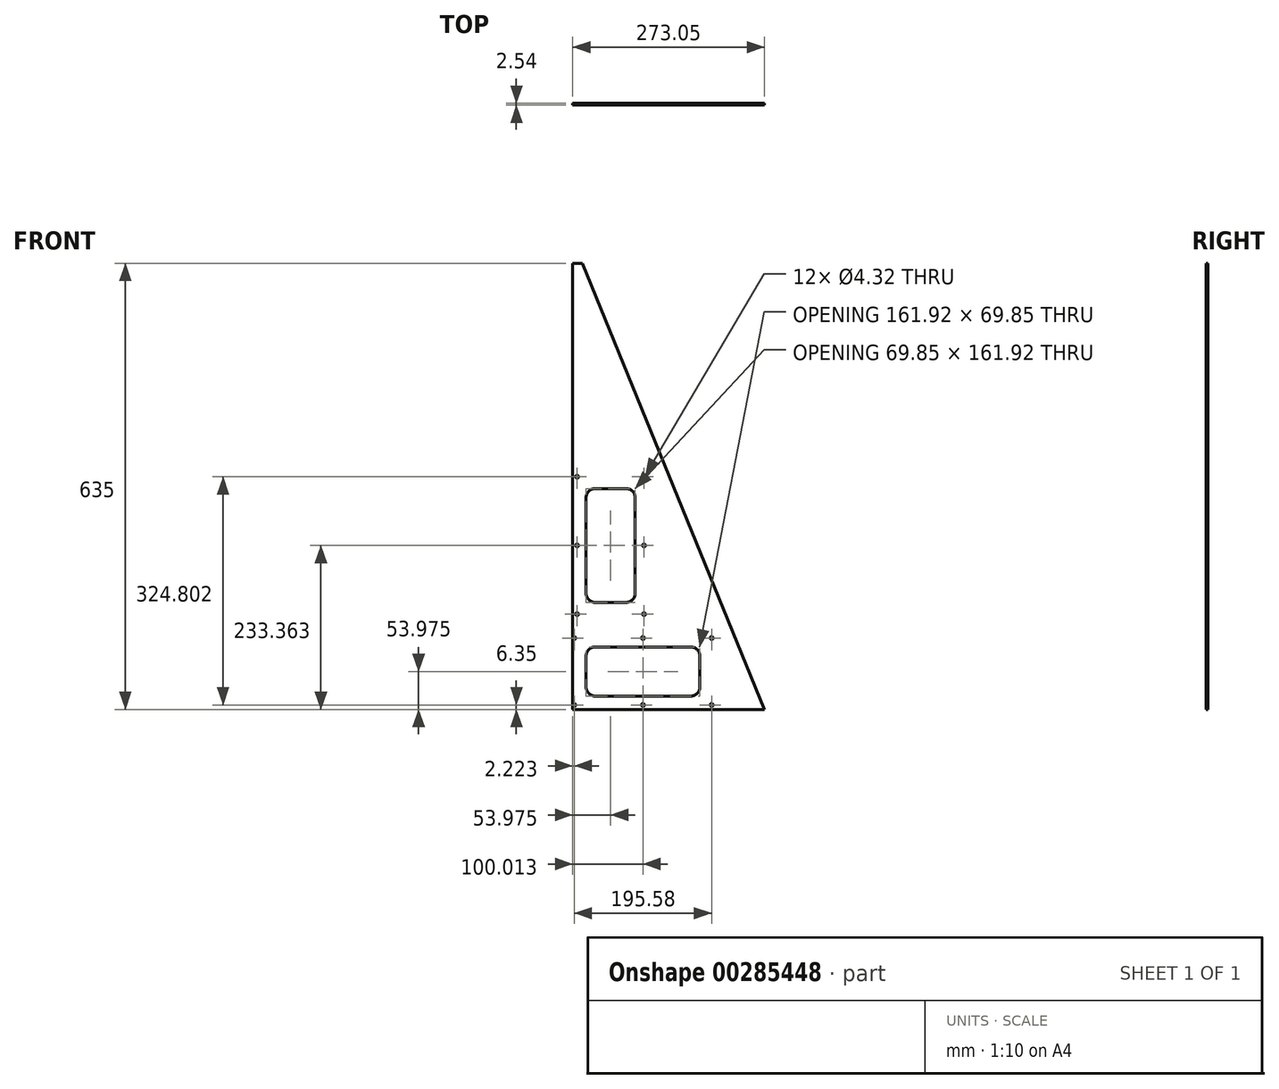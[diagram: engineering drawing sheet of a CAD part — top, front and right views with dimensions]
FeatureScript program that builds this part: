
annotation { "Feature Type Name" : "Feature", "Feature Type Description" : "" }
export const myFeature = defineFeature(function(context is Context, id is Id, definition is map)
    precondition{}
    {
        {
            var Q0;
            Q0=qCreatedBy(makeId("Front.planeOp"),FACE);
            var sketch = newSketch(context, id + "F0", { "sketchPlane" : qUnion([Q0])});
            skLineSegment(sketch, "E0", {"start": v(0, 0) * mm, "end": v(0, 635) * mm});
            skArc(sketch, "E1.MirrorCS", {"start": v(31.75, 19.05) * mm, "mid": v(22.77, 22.77) * mm, "end": v(19.05, 31.75) * mm});
            skArc(sketch, "E2.MirrorCS", {"start": v(168.28, 88.9) * mm, "mid": v(177.26, 85.18) * mm, "end": v(180.97, 76.2) * mm});
            skArc(sketch, "E3.MirrorCS", {"start": v(19.05, 76.2) * mm, "mid": v(22.77, 85.18) * mm, "end": v(31.75, 88.9) * mm});
            skArc(sketch, "E4.MirrorCS", {"start": v(31.75, 152.4) * mm, "mid": v(22.77, 156.12) * mm, "end": v(19.05, 165.1) * mm});
            skArc(sketch, "E5.MirrorCS", {"start": v(19.05, 301.63) * mm, "mid": v(22.77, 310.6) * mm, "end": v(31.75, 314.33) * mm});
            skArc(sketch, "E6.MirrorCS", {"start": v(180.97, 31.75) * mm, "mid": v(177.26, 22.77) * mm, "end": v(168.28, 19.05) * mm});
            skArc(sketch, "E7.MirrorCS", {"start": v(76.2, 314.33) * mm, "mid": v(85.18, 310.6) * mm, "end": v(88.9, 301.63) * mm});
            skArc(sketch, "E8.MirrorCS", {"start": v(88.9, 165.1) * mm, "mid": v(85.18, 156.12) * mm, "end": v(76.2, 152.4) * mm});
            skLineSegment(sketch, "E9.MirrorCS", {"start": v(0, 635) * mm, "end": v(14.02, 635) * mm});
            skLineSegment(sketch, "E10.MirrorCS", {"start": v(76.2, 152.4) * mm, "end": v(31.75, 152.4) * mm});
            skLineSegment(sketch, "E11.MirrorCS", {"start": v(180.97, 76.2) * mm, "end": v(180.97, 31.75) * mm});
            skLineSegment(sketch, "E12.MirrorCS", {"start": v(168.28, 88.9) * mm, "end": v(31.75, 88.9) * mm});
            skLineSegment(sketch, "E13.MirrorCS", {"start": v(19.05, 76.2) * mm, "end": v(19.05, 31.75) * mm});
            skLineSegment(sketch, "E14.MirrorCS", {"start": v(273.05, 0) * mm, "end": v(0, 0) * mm});
            skLineSegment(sketch, "E15.MirrorCS", {"start": v(168.28, 19.05) * mm, "end": v(31.75, 19.05) * mm});
            skLineSegment(sketch, "E16.MirrorCS", {"start": v(14.02, 635) * mm, "end": v(273.05, 0) * mm});
            skLineSegment(sketch, "E17.MirrorCS", {"start": v(76.2, 314.33) * mm, "end": v(31.75, 314.33) * mm});
            skPoint(sketch, "E18.MirrorP", {"position": v(19.05, 301.63) * mm});
            skLineSegment(sketch, "E19.MirrorCS", {"start": v(88.9, 165.1) * mm, "end": v(88.9, 301.63) * mm});
            skPoint(sketch, "E20.MirrorP", {"position": v(88.9, 301.63) * mm});
            skLineSegment(sketch, "E21.MirrorCS", {"start": v(19.05, 165.1) * mm, "end": v(19.05, 301.63) * mm});
            skSolve(sketch);
        }
        {
            var Q0;
            Q0=qSketchRegion(id+"F0",true);
            extrude(context, id + "F1", {"entities" : qUnion([Q0]), "depth" : 2.54 * mm});
        }
        {
            var Q0;
            Q0=makeQuery(id+"F1.opExtrude","CAP_FACE",FACE,{"disambiguationData":[OSD([sQuery(id+"F0.wireOp",EDGE,"E0"),sQuery(id+"F0.wireOp",EDGE,"E1.MirrorCS"),sQuery(id+"F0.wireOp",EDGE,"E2.MirrorCS"),sQuery(id+"F0.wireOp",EDGE,"E3.MirrorCS"),sQuery(id+"F0.wireOp",EDGE,"E4.MirrorCS"),sQuery(id+"F0.wireOp",EDGE,"E5.MirrorCS"),sQuery(id+"F0.wireOp",EDGE,"E6.MirrorCS"),sQuery(id+"F0.wireOp",EDGE,"E7.MirrorCS"),sQuery(id+"F0.wireOp",EDGE,"E8.MirrorCS"),sQuery(id+"F0.wireOp",EDGE,"E9.MirrorCS"),sQuery(id+"F0.wireOp",EDGE,"E10.MirrorCS"),sQuery(id+"F0.wireOp",EDGE,"E11.MirrorCS"),sQuery(id+"F0.wireOp",EDGE,"E12.MirrorCS"),sQuery(id+"F0.wireOp",EDGE,"E13.MirrorCS"),sQuery(id+"F0.wireOp",EDGE,"E14.MirrorCS"),sQuery(id+"F0.wireOp",EDGE,"E15.MirrorCS"),sQuery(id+"F0.wireOp",EDGE,"E16.MirrorCS"),sQuery(id+"F0.wireOp",EDGE,"E17.MirrorCS"),sQuery(id+"F0.wireOp",EDGE,"E19.MirrorCS"),sQuery(id+"F0.wireOp",EDGE,"E21.MirrorCS")])],"isStart":false});
            var sketch = newSketch(context, id + "F2", { "sketchPlane" : qUnion([Q0])});
            skPoint(sketch, "E22", {"position": v(2.22, 101.6) * mm});
            skPoint(sketch, "E23", {"position": v(100.01, 101.6) * mm});
            skPoint(sketch, "E24", {"position": v(197.8, 101.6) * mm});
            skPoint(sketch, "E25", {"position": v(197.8, 6.35) * mm});
            skPoint(sketch, "E26", {"position": v(100.01, 6.35) * mm});
            skPoint(sketch, "E27", {"position": v(2.22, 6.35) * mm});
            skLineSegment(sketch, "E28", {"start": v(100.01, 88.9) * mm, "end": v(100.01, 19.05) * mm, "construction": true});
            skPoint(sketch, "E29", {"position": v(6.35, 135.57) * mm});
            skPoint(sketch, "E30", {"position": v(6.35, 233.36) * mm});
            skPoint(sketch, "E31", {"position": v(6.35, 331.15) * mm});
            skPoint(sketch, "E32", {"position": v(101.6, 331.15) * mm});
            skPoint(sketch, "E33", {"position": v(101.6, 233.36) * mm});
            skPoint(sketch, "E34", {"position": v(101.6, 135.57) * mm});
            skLineSegment(sketch, "E35", {"start": v(19.05, 233.36) * mm, "end": v(88.9, 233.36) * mm, "construction": true});
            skSolve(sketch);
        }
        {
            var Q0;
            Q0=sQuery(id+"F2.wireOp",VERTEX,"E31");
            var Q1;
            Q1=sQuery(id+"F2.wireOp",VERTEX,"E32");
            var Q2;
            Q2=sQuery(id+"F2.wireOp",VERTEX,"E33");
            var Q3;
            Q3=sQuery(id+"F2.wireOp",VERTEX,"E30");
            var Q4;
            Q4=sQuery(id+"F2.wireOp",VERTEX,"E29");
            var Q5;
            Q5=sQuery(id+"F2.wireOp",VERTEX,"E34");
            var Q6;
            Q6=sQuery(id+"F2.wireOp",VERTEX,"E22");
            var Q7;
            Q7=sQuery(id+"F2.wireOp",VERTEX,"E27");
            var Q8;
            Q8=sQuery(id+"F2.wireOp",VERTEX,"E26");
            var Q9;
            Q9=sQuery(id+"F2.wireOp",VERTEX,"E23");
            var Q10;
            Q10=sQuery(id+"F2.wireOp",VERTEX,"E24");
            var Q11;
            Q11=sQuery(id+"F2.wireOp",VERTEX,"E25");
            var Q12;
            Q12=makeQuery(id+"F1.opExtrude","SWEPT_BODY",BODY,{"disambiguationData":[OSD([sQuery(id+"F0.wireOp",EDGE,"E0"),sQuery(id+"F0.wireOp",EDGE,"E1.MirrorCS"),sQuery(id+"F0.wireOp",EDGE,"E2.MirrorCS"),sQuery(id+"F0.wireOp",EDGE,"E3.MirrorCS"),sQuery(id+"F0.wireOp",EDGE,"E4.MirrorCS"),sQuery(id+"F0.wireOp",EDGE,"E5.MirrorCS"),sQuery(id+"F0.wireOp",EDGE,"E6.MirrorCS"),sQuery(id+"F0.wireOp",EDGE,"E7.MirrorCS"),sQuery(id+"F0.wireOp",EDGE,"E8.MirrorCS"),sQuery(id+"F0.wireOp",EDGE,"E9.MirrorCS"),sQuery(id+"F0.wireOp",EDGE,"E10.MirrorCS"),sQuery(id+"F0.wireOp",EDGE,"E11.MirrorCS"),sQuery(id+"F0.wireOp",EDGE,"E12.MirrorCS"),sQuery(id+"F0.wireOp",EDGE,"E13.MirrorCS"),sQuery(id+"F0.wireOp",EDGE,"E14.MirrorCS"),sQuery(id+"F0.wireOp",EDGE,"E15.MirrorCS"),sQuery(id+"F0.wireOp",EDGE,"E16.MirrorCS"),sQuery(id+"F0.wireOp",EDGE,"E17.MirrorCS"),sQuery(id+"F0.wireOp",EDGE,"E19.MirrorCS"),sQuery(id+"F0.wireOp",EDGE,"E21.MirrorCS")])]});
            hole(context, id + "F3", {"style" : HoleStyle.SIMPLE, "endStyle" : HoleEndStyle.THROUGH, "standardTappedOrClearance" : lookupTablePath({ "standard" : "ANSI", "fit" : "Close", "size" : "#8", "type" : "Clearance" }), "standardBlindInLast" : lookupTablePath({ "fit" : "Close", "standard" : "ANSI", "size" : "#8", "type" : "Clearance" }), "holeDiameter" : 4.32 * mm, "isTappedThrough" : true, "tappedDepth" : 2.4 * mm, "tapClearance" : 3, "startFromSketch" : true, "locations" : qUnion([Q0, Q1, Q2, Q3, Q4, Q5, Q6, Q7, Q8, Q9, Q10, Q11]), "scope" : qUnion([Q12])});
        }
    });
